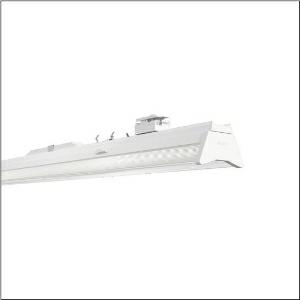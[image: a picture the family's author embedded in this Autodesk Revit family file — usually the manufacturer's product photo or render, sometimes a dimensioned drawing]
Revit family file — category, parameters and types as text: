
# Revit family: licross_r__21_performance_mo_52td167n445g_3390
name_source: partatom
category: Lighting Fixtures
units: mm (PartAtom-declared; Revit-internal decimal feet)

## family parameters
Cut with Voids When Loaded = No
Host = Face
Light Source = No
Part Type = Normal
Room Calculation Point = No
Round Connector Dimension = Use Diameter
Shared = No

## types (1)
- Licross® 21 Performance MO (1 x LED, 4580 lm, 24.7 W, 4000K)
    Apparent Load = 25 VA
    CIE Flux Codes = 66 88 96 79 100
    Color Rendering = 80
    Color Temperature = 4000K
    Default Elevation = 1800 mm
    Description = Licross® 21 Performance MO, luminaire insert, of sheet steel, galvanised, coil coated, white, length: 1.500mm, width: 120mm, height: 123mm, LED rated luminous flux: 4.580lm, light colour: 840, control gear: ON/OFF, with plug, 3-pole, with phase selection, mains connection: 220..240V, AC, 50/60Hz, rated input power: 25W, halogen-free wiring, primary light control with lens, of plastic, primary optical cover: cover, of PMMA, CAT 2 (L<= 3000cd/m²), light emission: direct/indirect distribution, primary light characteristic: symmetric, protection rating (complete): IP54, insulation class (complete): insulation class I (protective earthing), certification: CE, ENEC, UKCA, protection symbol: D if used in an environment with non-conductive dust loads with corresponding accessories, impact resistance: IK06, permissible ambient temperature for indoor applications: -35..+55°C, corresponds to IFS (International Featured Standards) requirements for safety and quality in the food industry, reducing of maximum allowable ambient temperature of 5°C with ceiling mounting, LABS conformity tested according to VDMA 24364:2018-05, packaging unit: 1 piece
    Height = 114 mm
    Lamp = 1 x LED
    Lamp Light Flux = 4580 lm
    Lamp Power = 24.7 W
    Lamp count = 1
    Length = 1500 mm
    Luminous efficacy = 185 lm/W
    Manufacturer = Siteco
    ModVariant = No
    Model = 52TD167N445G
    Mounting Place = Ceiling
    Mounting Type = Pendant
    Number of Poles = 1
    OnlyDefault = Yes
    Power Factor = 1
    Product Name = Licross® 21 Performance MO
    Product group = luminaire insert
    ProductGroupID = 902
    Protection Class = Protection class I
    Protection Degree = IP 54
    RLX_Detail_Level = 1
    RLX_Emergency_Light_Flux = 0 lm
    RLX_Emergency_Type = 0
    RLX_Emergency_Type_DB = No
    RlxData = <blob elided: 30513 chars, md5=f69539d4>
    Socket = socket
    Standby Power = 0 W
    System Light Flux = 4580 lm
    System Power = 25 W
    Type Comments = Product without accessories
    Type Image = l_1256138.jpg
    URL = http://relux.com
    VarID = ---
    Voltage = 0 V
    Weight = 0.00 kg
    Width = 120 mm

## geometry (parser evidence)
native form markers: Blend x4, Sweep x12
no freeform markers — native parametric forms only
